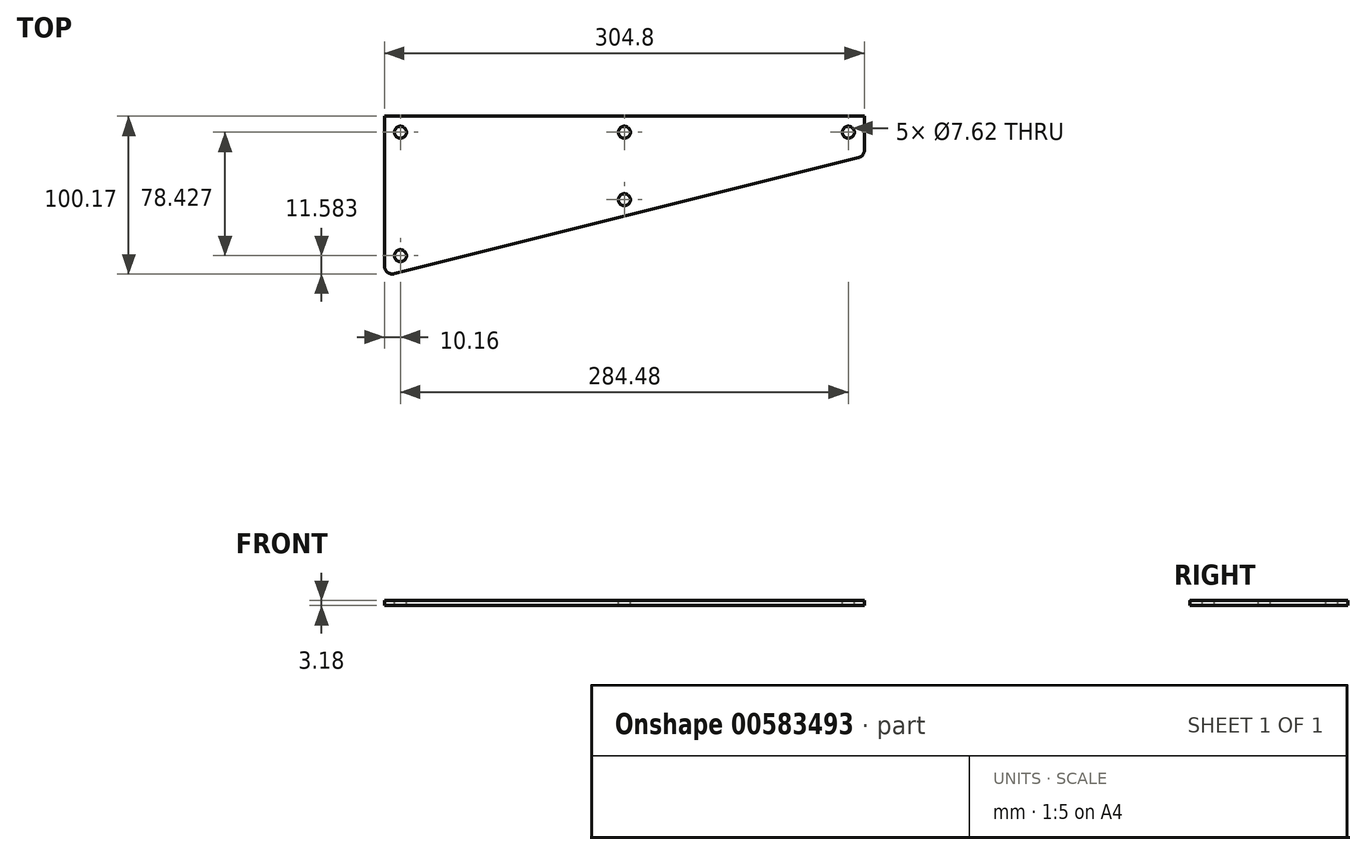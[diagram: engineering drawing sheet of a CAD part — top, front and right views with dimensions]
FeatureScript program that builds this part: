
annotation { "Feature Type Name" : "Feature", "Feature Type Description" : "" }
export const myFeature = defineFeature(function(context is Context, id is Id, definition is map)
    precondition{}
    {
        {
            var Q0;
            Q0=qCreatedBy(makeId("Top.planeOp"),FACE);
            var sketch = newSketch(context, id + "F0", { "sketchPlane" : qUnion([Q0])});
            skLineSegment(sketch, "E0", {"start": v(0, 0) * mm, "end": v(-304.8, 0) * mm});
            skLineSegment(sketch, "E1", {"start": v(0, 0) * mm, "end": v(0, -21.43) * mm});
            skLineSegment(sketch, "E2", {"start": v(-304.8, 0) * mm, "end": v(-304.8, -95.1) * mm});
            skLineSegment(sketch, "E3", {"start": v(-298.49, -100.02) * mm, "end": v(-3.85, -26.36) * mm});
            skPoint(sketch, "E4.visualSharp", {"position": v(-304.8, -101.6) * mm});
            skArc(sketch, "E4.filletArc", {"start": v(-304.8, -95.1) * mm, "mid": v(-302.85, -99.1) * mm, "end": v(-298.49, -100.02) * mm});
            skPoint(sketch, "E5.visualSharp", {"position": v(0, -25.4) * mm});
            skArc(sketch, "E5.filletArc", {"start": v(-3.85, -26.36) * mm, "mid": v(-1.08, -24.56) * mm, "end": v(0, -21.43) * mm});
            skSolve(sketch);
        }
        {
            var Q0;
            Q0=makeQuery(id+"F0.imprint","IMPRINT",FACE,{"disambiguationData":[TD([[makeQuery(id+"F0.imprint","IMPRINT",EDGE,{"derivedFrom":sQuery(id+"F0.wireOp",EDGE,"E0")}),1.0]])]});
            extrude(context, id + "F1", {"entities" : qUnion([Q0]), "depth" : 3.17 * mm, "offsetDistance" : 25.4 * mm});
        }
        {
            var Q0;
            Q0=makeQuery(id+"F1.opExtrude","CAP_FACE",FACE,{"disambiguationData":[OSD([sQuery(id+"F0.wireOp",EDGE,"E0"),sQuery(id+"F0.wireOp",EDGE,"E1"),sQuery(id+"F0.wireOp",EDGE,"E2"),sQuery(id+"F0.wireOp",EDGE,"E3"),sQuery(id+"F0.wireOp",EDGE,"E4.filletArc"),sQuery(id+"F0.wireOp",EDGE,"E5.filletArc")])],"isStart":false});
            var sketch = newSketch(context, id + "F2", { "sketchPlane" : qUnion([Q0])});
            skLineSegment(sketch, "E6", {"start": v(-289.86, -10.16) * mm, "end": v(-11.84, -10.16) * mm, "construction": true});
            skLineSegment(sketch, "E7", {"start": v(-294.95, -88.66) * mm, "end": v(-102.42, -40.53) * mm, "construction": true});
            skCircle(sketch, "E8", {"center": v(-10.16, -10.16) * mm, "radius": 3.81 * mm});
            skCircle(sketch, "E9", {"center": v(-152.4, -10.16) * mm, "radius": 3.81 * mm});
            skCircle(sketch, "E10", {"center": v(-294.64, -10.16) * mm, "radius": 3.81 * mm});
            skCircle(sketch, "E11", {"center": v(-294.64, -88.59) * mm, "radius": 3.81 * mm});
            skCircle(sketch, "E12", {"center": v(-152.4, -53.03) * mm, "radius": 3.8 * mm});
            skSolve(sketch);
        }
        {
            var Q0;
            Q0=makeQuery(id+"F2.imprint","IMPRINT",FACE,{"disambiguationData":[TD([[makeQuery(id+"F2.imprint","IMPRINT",EDGE,{"derivedFrom":sQuery(id+"F2.wireOp",EDGE,"E10")}),1.0]])]});
            var Q1;
            Q1=makeQuery(id+"F2.imprint","IMPRINT",FACE,{"disambiguationData":[TD([[makeQuery(id+"F2.imprint","IMPRINT",EDGE,{"derivedFrom":sQuery(id+"F2.wireOp",EDGE,"E9")}),1.0]])]});
            var Q2;
            Q2=makeQuery(id+"F2.imprint","IMPRINT",FACE,{"disambiguationData":[TD([[makeQuery(id+"F2.imprint","IMPRINT",EDGE,{"derivedFrom":sQuery(id+"F2.wireOp",EDGE,"E12")}),1.0]])]});
            var Q3;
            Q3=makeQuery(id+"F2.imprint","IMPRINT",FACE,{"disambiguationData":[TD([[makeQuery(id+"F2.imprint","IMPRINT",EDGE,{"derivedFrom":sQuery(id+"F2.wireOp",EDGE,"E11")}),1.0]])]});
            var Q4;
            Q4=makeQuery(id+"F2.imprint","IMPRINT",FACE,{"disambiguationData":[TD([[makeQuery(id+"F2.imprint","IMPRINT",EDGE,{"derivedFrom":sQuery(id+"F2.wireOp",EDGE,"E8")}),1.0]])]});
            extrude(context, id + "F3", {"entities" : qUnion([Q0, Q1, Q2, Q3, Q4]), "operationType" : NewBodyOperationType.REMOVE, "oppositeDirection" : true, "depth" : 25.4 * mm, "offsetDistance" : 25.4 * mm});
        }
    });
